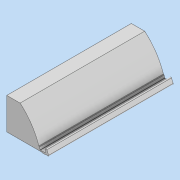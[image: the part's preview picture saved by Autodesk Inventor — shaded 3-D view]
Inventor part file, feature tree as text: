
AUTODESK INVENTOR PART (.ipt)
format: ipt  version: 2020 (Build 240168000, 168)  size: 148,480 bytes
history: native  units: mm
features: other x1, sweep x1, fillet x1, sketch x1
ambient origin geometry x8: Origin, YZ Plane, XZ Plane, XY Plane, X Axis, Y Axis, Z Axis, Center Point
bodies: Body1 (feature_tree)
feature tree (4):
  other  "實體1"
  sweep  "掃掠1"
  fillet  "圓角1"  Radius=1.7mm
  sketch  "草圖3"
